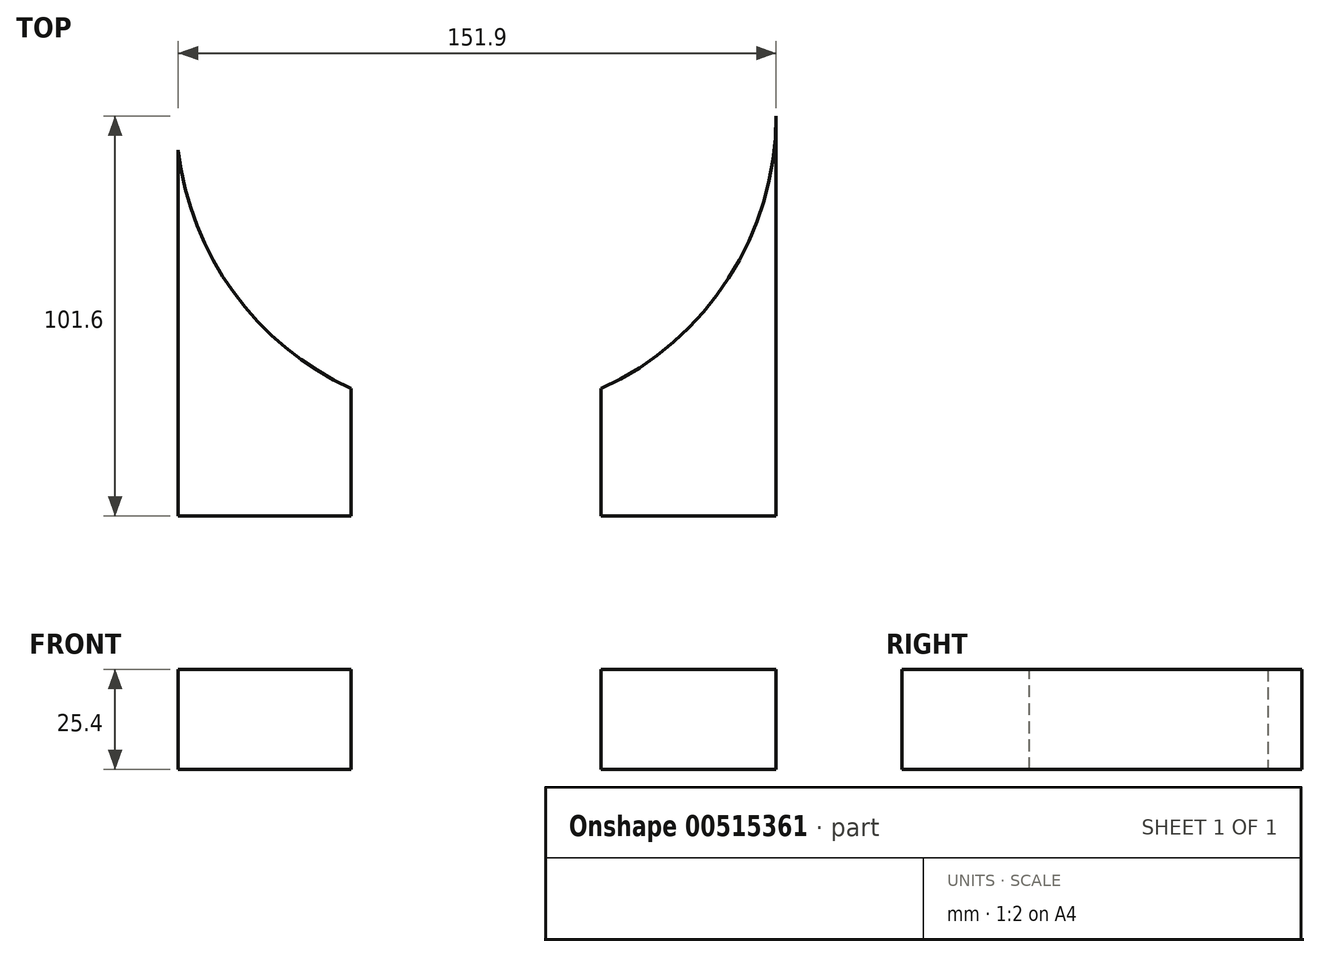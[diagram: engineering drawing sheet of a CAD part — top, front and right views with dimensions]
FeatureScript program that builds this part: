
annotation { "Feature Type Name" : "Feature", "Feature Type Description" : "" }
export const myFeature = defineFeature(function(context is Context, id is Id, definition is map)
    precondition{}
    {
        {
            var Q0;
            Q0=qCreatedBy(makeId("Top.planeOp"),FACE);
            var sketch = newSketch(context, id + "F0", { "sketchPlane" : qUnion([Q0])});
            skCircle(sketch, "E0", {"center": v(0, 0) * mm, "radius": 76.2 * mm});
            skLineSegment(sketch, "E1.bottom", {"start": v(-76.2, 0) * mm, "end": v(76.2, 0) * mm});
            skLineSegment(sketch, "E1.top", {"start": v(-76.2, 0) * mm, "end": v(76.2, 0) * mm});
            skLineSegment(sketch, "E1.left", {"start": v(-76.2, 0) * mm, "end": v(-76.2, 0) * mm});
            skLineSegment(sketch, "E1.right", {"start": v(76.2, 0) * mm, "end": v(76.2, 0) * mm});
            skLineSegment(sketch, "E2.bottom", {"start": v(76.2, 0) * mm, "end": v(-75.7, 0) * mm});
            skLineSegment(sketch, "E2.top", {"start": v(76.2, -101.6) * mm, "end": v(-75.7, -101.6) * mm});
            skLineSegment(sketch, "E2.left", {"start": v(76.2, 0) * mm, "end": v(76.2, -101.6) * mm});
            skLineSegment(sketch, "E2.right", {"start": v(-75.7, 0) * mm, "end": v(-75.7, -101.6) * mm});
            skSolve(sketch);
        }
        {
            var Q0;
            {var subQ0=sQuery(id+"F0.wireOp",EDGE,"E1.top");Q0=makeQuery(id+"F0.imprint","IMPRINT",FACE,{"disambiguationData":[TD([[makeQuery(id+"F0.imprint","IMPRINT",EDGE,{"derivedFrom":subQ0}),1.0]])]});}
            var Q1;
            {var subQ0=sQuery(id+"F0.wireOp",EDGE,"E2.bottom");Q1=makeQuery(id+"F0.imprint","IMPRINT",FACE,{"disambiguationData":[TD([[makeQuery(id+"F0.imprint","IMPRINT",EDGE,{"derivedFrom":subQ0}),1.0]])]});}
            var Q2;
            {var subQ4=sQuery(id+"F0.wireOp",EDGE,"E2.top");Q2=makeQuery(id+"F0.imprint","IMPRINT",FACE,{"disambiguationData":[TD([[makeQuery(id+"F0.imprint","IMPRINT",EDGE,{"derivedFrom":subQ4}),-1.0]])]});}
            extrude(context, id + "F1", {"entities" : qUnion([Q0, Q1, Q2]), "depth" : 25.4 * mm, "offsetDistance" : 25.4 * mm});
        }
        {
            var Q0;
            Q0=makeQuery(id+"F1.opExtrude","CAP_FACE",FACE,{"disambiguationData":[OSD([sQuery(id+"F0.wireOp",EDGE,"E0"),sQuery(id+"F0.wireOp",EDGE,"E1.top"),sQuery(id+"F0.wireOp",EDGE,"E2.top"),sQuery(id+"F0.wireOp",EDGE,"E2.left"),sQuery(id+"F0.wireOp",EDGE,"E2.right")])],"isStart":false});
            var sketch = newSketch(context, id + "F2", { "sketchPlane" : qUnion([Q0])});
            skCircle(sketch, "E3", {"center": v(0, 0) * mm, "radius": 50.8 * mm});
            skSolve(sketch);
        }
        {
            var Q0;
            Q0=makeQuery(id+"F2.imprint","IMPRINT",FACE,{"disambiguationData":[TD([[makeQuery(id+"F2.imprint","IMPRINT",EDGE,{"derivedFrom":sQuery(id+"F2.wireOp",EDGE,"E3")}),1.0]])]});
            extrude(context, id + "F3", {"entities" : qUnion([Q0]), "operationType" : NewBodyOperationType.REMOVE, "oppositeDirection" : true, "depth" : 25.4 * mm, "offsetDistance" : 25.4 * mm});
        }
        {
            var Q0;
            Q0=makeQuery(id+"F1.opExtrude","CAP_FACE",FACE,{"disambiguationData":[OSD([sQuery(id+"F0.wireOp",EDGE,"E0"),sQuery(id+"F0.wireOp",EDGE,"E1.top"),sQuery(id+"F0.wireOp",EDGE,"E2.top"),sQuery(id+"F0.wireOp",EDGE,"E2.left"),sQuery(id+"F0.wireOp",EDGE,"E2.right")])],"isStart":false});
            var sketch = newSketch(context, id + "F4", { "sketchPlane" : qUnion([Q0])});
            skLineSegment(sketch, "E4.bottom", {"start": v(-31.75, -101.6) * mm, "end": v(31.75, -101.6) * mm});
            skLineSegment(sketch, "E4.top", {"start": v(-31.75, -63.5) * mm, "end": v(31.75, -63.5) * mm});
            skLineSegment(sketch, "E4.left", {"start": v(-31.75, -101.6) * mm, "end": v(-31.75, -63.5) * mm});
            skLineSegment(sketch, "E4.right", {"start": v(31.75, -101.6) * mm, "end": v(31.75, -63.5) * mm});
            skSolve(sketch);
        }
        {
            var Q0;
            Q0=makeQuery(id+"F4.imprint","IMPRINT",FACE,{"disambiguationData":[TD([[makeQuery(id+"F4.imprint","IMPRINT",EDGE,{"derivedFrom":sQuery(id+"F4.wireOp",EDGE,"E4.bottom")}),-1.0]])]});
            extrude(context, id + "F5", {"entities" : qUnion([Q0]), "operationType" : NewBodyOperationType.REMOVE, "oppositeDirection" : true, "depth" : 25.4 * mm, "offsetDistance" : 25.4 * mm});
        }
    });
